# Revit family: QF_ELECTROLUXPROFESSIONAL_1LSN2C_WH6-6_E
name_source: partatom
category: Attrezzature speciali
units: mm (PartAtom-declared; Revit-internal decimal feet)

## family parameters
Basato su piano di lavoro = No
Condiviso = No
Punto di calcolo locali = No
Quota connettore circolare = Usa diametro
Sempre verticale = Sì
Taglio con vuoti quando caricato = No
Tipo di parte = Normale

## types (139) — shared parameters
Depth Actual = 595 mm  [stored 1.9521 ft]
Height Actual = 832 mm
Latent Heat Output = 0.0
Length Actual = 681 mm  [stored 2.23425 ft]
Modello = WH6-6
Produttore = Electrolux Professional
Sensible Heat Output = 0.0
URL = www.electroluxprofessional.com
Weight = 58
zero-valued in all types: Gas KW, Prospetto di default, Steam Pounds per Hour

## per-type parameters (varying)
| type | Cycle | Descrizione | Item Number | Phase | Volts | Watts |
| 9863430007 | 50 Hz | WASHER EXTRACTOR WH6-6 6KG/13LB EL 4,4KW 380-400/220-230/50/3N/1N COMPASS PRO 6H12 2.I/O 2xWATER POWDER+5xLIQ. QC VA... | 1L0ECD | 3 | 400 V | 2400 W |
| 9863430017 | 50 Hz | WASHER WH6-6 6KG EL 4,4KW 380-400/220-230/50/3N/1N COMPASS PRO 6L25 ML 2xWATER POWDER+5xLIQ. PUMP SILVER EXT.PM. 2.I/O | 1L0ECN | 3 | 400 V | 2400 W |
| 9863430207 | 60 Hz | WASHER EXTRACTOR WH6-6 MARINE 6KG/13LB EL 4,4KW 480/60/3 COMPASS PRO 6G07 2.I/O 2xWATER POWDER+5xLIQ. VALV.OPEN SLVR... | 1L0H5S | 3 | 480 V | 4600 W |
| 9863430217 | 60 Hz | Model: WH6-6 TYPE FAMILY W555H17 CH-EN MARINE 6KG EL 4KW 440/60/3 CPR 6G07 ML 2xWATER POWDER VALV.OPEN SILVER TRAFO | 1LT66F | 3 | 440 V | 4200 W |
| 9863430227 | 60 Hz | WASHER EXTRACTOR WH6-6 6KG/13LB EL 3,3KW 380-400/220-230/60/3N/1N COMPASS PRO 6G01 2.I/O 2xWATER POWDER+5xLIQ. VALV.... | 1LT6GB | 3 | 400 V | 3500 W |
| 9863430193 | 60 Hz | WASHER EXTRACTOR WH6-6 MARINE 6KG/13LB EL 4KW 440/60/3 COMPASS PRO 6G07 2xWATER POWDER VALV.OPEN SLVR/SLVR INS. TRAFO | 1L0GUG | 3 | 440 V | 4200 W |
| 9863430173 | 50 Hz | WASHER EXTRACTOR WH6-6 6KG/13LB NO HEAT 220-240/50/1N COMPASS PRO 6L25 2.I/O 2xWATER POWDER+5xLIQ. PUMP SST/SLVR | 1L999M | 1 | 240 V | 500 W |
| 9863430143 | 60 Hz | WASHER EXTRACTOR WH6-6 MARINE 6KG/13LB EL 4KW 440/60/3 COMPASS PRO 6G07 2xWATER POWDER VALV.OPEN SLVR/SLVR TRAFO | 1LA1AT | 3 | 440 V | 4200 W |
| 9863430153 | 50 Hz | WASHER EXTRACTOR WH6-6 6KG/13LB EL 2,8KW 220-240/50/1N COMPASS PRO 6G25 2.I/O 2xWATER POWDER+5xLIQ. PUMP SLVR/SLVR 1... | 1LA21G | 1 | 240 V | 3000 W |
| 9863430113 | 60 Hz | WASHER EXTRACTOR WH6-6 MARINE 6KG/13LB EL 4,4KW 380-400/220-230/60/3N/1N COMPASS PRO 6G27 2.I/O 2xWATER POWDER+5xLIQ... | 1LSNGY | 3 | 400 V | 2400 W |
| 9863430088 | 60 Hz | WASHER EXTRACTOR WH6-6 6KG/13LB EL 2,8KW 208-240/60/3 COMPASS PRO 6L01 2.I/O 2xWATER POWDER+5xLIQ. VALV.OPEN SLVR/SLVR | 1L0EL6 | 3 | 240 V | 3000 W |
| 9863430098 | 50 Hz | WASHER EXTRACTOR WH6-6 6KG/13LB EL 4,4KW 380-400/220-230/50/3N/1N COMPASS PRO 6H12 2.I/O 2xWATER POWDER+5xLIQ. QC PU... | 1LSNBM | 3 | 400 V | 2400 W |
| 9863430078 | 50 Hz | WASHER EXTRACTOR WH6-6 6KG/13LB EL 4,4KW 380-400/220-230/50/3N/1N COMPASS PRO 6A01 2xWATER POWDER VALV.OPEN SLVR/SLV... | 1LSN6B | 3 | 400 V | 2400 W |
| 9863430058 | 50 Hz | WASHER EXTRACTOR WH6-6 6KG/13LB EL 4,4KW 380-400/220-230/50/3N/1N COMPASS PRO 6A01 2xWATER POWDER EL.VALV.OPEN SLVR/... | 1L80G7 | 3 | 400 V | 2400 W |
| 9863430028 | 60 Hz | WASHER EXTRACTOR WH6-6 MARINE 6KG/13LB EL 4KW 440/60/3 COMPASS PRO 6G27 2xWATER POWDER PUMP SLVR/SLVR TRAFO | 1L0ED0 | 3 | 440 V | 4200 W |
| 9863430018 | 50 Hz | WASHER EXTRACTOR WH6-6 6KG/13LB EL 4,4KW 380-400/220-230/50/3N/1N COMPASS PRO 6M14 2.I/O 2xWATER POWDER+5xLIQ. QC EL... | 1L0ECP | 3 | 400 V | 2400 W |
| 9863430083 | 60 Hz | WASHER EXTRACTOR WH6-6 6KG/13LB EL 2,8KW 208-240/60/1 COMPASS PRO 6L01 2.I/O 2xWATER POWDER+5xLIQ. VALV.OPEN SLVR/SLVR | 1L0EK6 | 1 | 240 V | 3000 W |
| 9863430063 | 60 Hz | WASHER EXTRACTOR WH6-6 6KG/13LB NO HEAT 120/60/1N COMPASS PRO 6L33 2.I/O 2xWATER POWDER+5xLIQ. PUMP SLVR/SLVR TRAFO | 1L80GF | 1 | 120 V | 600 W |
| 9863430186 | 60 Hz | WASHER EXTRACTOR WH6-6 MARINE 6KG/13LB EL 4KW 440/60/3 COMPASS PRO 6G27 2xWATER POWDER PUMP SLVR/SLVR TRAFO | 1L0GTB | 3 | 440 V | 4200 W |
| 9863430023 | 50 Hz | WASHER EXTRACTOR WH6-6 6KG/13LB EL 4,4KW 380-400/220-230/50/3N/1N COMPASS PRO 6A01 2xWATER POWDER VALV.OPEN SLVR/SLV... | 1L0ECV | 3 | 400 V | 2400 W |
| 9863430166 | 60 Hz | WASHER EXTRACTOR WH6-6 MARINE 6KG/13LB EL 4,4KW 380-400/220-230/60/3N/1N COMPASS PRO 6G27 2xWATER POWDER PUMP SLVR/SLVR | 1L0GE6 | 3 | 400 V | 2400 W |
| 9863430176 | 50 Hz | WASHER EXTRACTOR WH6-6 6KG/13LB NO HEAT 220-240/50/1N COMPASS PRO 6G01 2xWATER POWDER VALV.OPEN SLVR/SLVR | 1L0GP0 | 1 | 240 V | 500 W |
| 9863430146 | 50 Hz | WASHER EXTRACTOR WH6-6 6KG/13LB EL 4,4KW 220-230/50/1N COMPASS PRO 6G01 2xWATER POWDER VALV.OPEN SLVR/SLVR | 1LA21A | 1 | 230 V | 4600 W |
| 9863430126 | 50 Hz | WASHER EXTRACTOR WH6-6 MARINE 6KG/13LB EL 3,3KW 380-400/50/3 COMPASS PRO 6G07 2.I/O 2xWATER POWDER+5xLIQ. EL.VALV.OP... | 1LSNRD | 3 | 400 V | 3500 W |
| 9863430196 | 50 Hz | WASHER EXTRACTOR WH6-6 6KG/13LB EL 3,3KW 380-400/220-230/50/3N/1N COMPASS PRO 6M17 2.I/O 2xWATER POWDER+5xLIQ. EL.VA... | 1LSPHT | 3 | 400 V | 3500 W |
| 9863430213 | 50 Hz | WASHER EXTRACTOR WH6-6 MARINE 6KG/13LB EL 3,6KW 380-415/50/3 COMPASS PRO 6G07 2.I/O 2xWATER POWDER+5xLIQ. QC VALV.OP... | 1LT65S | 3 | 415 V | 3800 W |
| 9863430064 | 60 Hz | WASHER EXTRACTOR WH6-6 6KG/13LB NO HEAT 120/60/1N COMPASS PRO 6L33 2xWATER POWDER VALV.OPEN SLVR/SLVR ELS-NETW. TRAFO | 1L80GG | 1 | 120 V | 600 W |
| 9863430044 | 50 Hz | WASHER EXTRACTOR WH6-6 6KG/13LB EL 3,3KW 200/50/60/3 COMPASS PRO 6H43 2.I/O 2xWATER POWDER+5xLIQ. VALV.OPEN SLVR/SLV... | 1L0EHE | 3 | 200 V | 3500 W |
| 9863430189 | 50 Hz | WASHER EXTRACTOR WH6-6 MARINE 6KG/13LB EL 3,3KW 380-400/50/3 COMPASS PRO 6G07 2.I/O 2xWATER POWDER+5xLIQ. EL.VALV.OP... | 1L0GTE | 3 | 400 V | 3500 W |
| 9863430024 | 60 Hz | WASHER EXTRACTOR WH6-6 MARINE 6KG/13LB EL 4KW 440/60/3 COMPASS PRO 6G07 2xWATER POWDER VALV.OPEN SLVR/SLVR INS. TRAFO | 1L0ECW | 3 | 440 V | 4200 W |
| 9863430034 | 60 Hz | WASHER WH6-6 MARINE 6KG EL 4KW 440/60/3 COMPASS PRO 6G07 ML 2xWATER POWDER+5xLIQ. VALV.OPEN SILVER QC 2.I/O TRAFO | 1L0ED5 | 3 | 440 V | 4200 W |
| 9863430169 | 60 Hz | WASHER EXTRACTOR WH6-6 MARINE 6KG/13LB EL 4,4KW 208-240/60/3 COMPASS PRO 6G27 2xWATER POWDER PUMP SLVR/SLVR | 1L0GHL | 3 | 240 V | 4600 W |
| 9863430014 | 50 Hz | WASHER EXTRACTOR WH6-6 6KG/13LB EL 4,4KW 380-400/220-230/50/3N/1N COMPASS PRO 6R01 2.I/O 2xWATER POWDER+5xLIQ. QC EL... | 1L0ECK | 3 | 400 V | 2400 W |
| 9863430199 | 50 Hz | WASHER EXTRACTOR WH6-6 6KG/13LB EL 3,3KW 200/50/60/3 COMPASS PRO 6H43 2xWATER POWDER VALV.OPEN SLVR/SLVR TRAFO | 1L0GY3 | 3 | 200 V | 3500 W |
| 9863430054 | 50 Hz | WASHER EXTRACTOR WH6-6 MARINE 6KG/13LB EL 3,3KW 380-400/50/3 COMPASS PRO 6G07 2.I/O 2xWATER POWDER+5xLIQ. VALV.OPEN ... | 1L80FY | 3 | 400 V | 3500 W |
| 9863430109 | 50 Hz | WASHER EXTRACTOR WH6-6 MARINE 6KG/13LB EL 4,4KW 220-230/50/3 COMPASS PRO 6G07 2xWATER POWDER VALV.OPEN SLVR/SLVR INS. | 1L0EPN | 3 | 230 V | 4600 W |
| 9863430119 | 50 Hz | WASHER EXTRACTOR WH6-6 6KG/13LB EL 4,4KW 220-230/50/3 COMPASS PRO 6A25 2.I/O 2xWATER POWDER+5xLIQ. PUMP SLVR/SLVR | 1L0FXT | 3 | 230 V | 4600 W |
| 9863430139 | 50 Hz | WASHER EXTRACTOR WH6-6 6KG/13LB EL 4,4KW 380-400/220-230/50/3N/1N COMPASS PRO 6G25 2.I/O 2xWATER POWDER+5xLIQ. QC PU... | 1LA215 | 3 | 400 V | 2400 W |
| 9863430149 | 50 Hz | WASHER EXTRACTOR WH6-6 MARINE 6KG/13LB EL 3,3KW 380-400/50/3 COMPASS PRO 6G07 2.I/O 2xWATER POWDER+5xLIQ. QC VALV.OP... | 1LA21C | 3 | 400 V | 3500 W |
| 9863430129 | 50 Hz | WASHER EXTRACTOR WH6-6 6KG/13LB EL 2,8KW 220-240/50/1N COMPASS PRO 6A25 2.I/O 2xWATER POWDER+5xLIQ. PUMP SLVR/SLVR | 1LSNXA | 1 | 240 V | 3000 W |
| 9863430182 | 50 Hz | WASHER EXTRACTOR WH6-6 6KG/13LB EL 4,4KW 380-400/220-230/50/3N/1N COMPASS PRO 6G01 2.I/O 2xWATER POWDER+5xLIQ. VALV.... | 1L0GT7 | 3 | 400 V | 2400 W |
| 9863430192 | 60 Hz | WASHER EXTRACTOR WH6-6 MARINE 6KG/13LB EL 4KW 440/60/3 COMPASS PRO 6G27 2.I/O 2xWATER POWDER+5xLIQ. PUMP SLVR/SLVR T... | 1L0GUF | 3 | 440 V | 4200 W |
| 9863430162 | 50 Hz | WASHER EXTRACTOR WH6-6 6KG/13LB NO HEAT 220-240/50/1N COMPASS PRO 6G01 2.I/O 2xWATER POWDER+5xLIQ. VALV.OPEN SLVR/SLVR | 1LSPAY | 1 | 240 V | 500 W |
| 9863430172 | 60 Hz | WASHER EXTRACTOR WH6-6 MARINE 6KG/13LB EL 4,4KW 220-230/60/3 COMPASS PRO 6G07 2.I/O 2xWATER POWDER+5xLIQ. VALV.OPEN ... | 1L0GL9 | 3 | 230 V | 4600 W |
| 9863430142 | 50 Hz | WASHER EXTRACTOR WH6-6 6KG/13LB EL 4,4KW 380-400/220-230/50/3N/1N COMPASS PRO 6L01 2.I/O 2xWATER POWDER+5xLIQ. VALV.... | 1LA217 | 3 | 400 V | 2400 W |
| 9863430218 | 50 Hz | Model: WH6-6 TYPE FAMILY W555H17 CH-EN 6 6KG EL 4,4KW 380-400/220-230/50/3N/1N COMPASS PRO 6G01 ML 2xWATER POWDER VALV.O | 1LT66K | 3 | 400 V | 2400 W |
| 9863430228 | 50 Hz | Model: WH6-6 TYPE FAMILY W555H17 CH-EN 6 6KG EL 4,4KW 380-400/220-230/50/3N/1N COMPASS PRO 6G01 ML 2xWATER POWDER VALV.O | 1LT6U8 | 3 | 230 V | 3500 W |
| 9863430080 | 50 Hz | WASHER EXTRACTOR WH6-6 6KG/13LB EL 4,4KW 380-400/220-230/50/3N/1N COMPASS PRO 6A01 2.I/O 2xWATER POWDER VALV.OPEN SL... | 1LSN6W | 3 | 400 V | 2400 W |
| 9863430070 | 60 Hz | WASHER EXTRACTOR WH6-6 MARINE 6KG/13LB EL 4KW 440/60/3 COMPASS PRO 6G07 2xWATER POWDER VALV.OPEN SST/SLVR INS. TRAFO | 1LSN53 | 3 | 440 V | 4200 W |
| 9863430185 | 50 Hz | WASHER EXTRACTOR WH6-6 6KG/13LB EL 4,4KW 240/50/1N COMPASS PRO 6H01 2.I/O 2xWATER POWDER+5xLIQ. EL.VALV.OPEN SLVR/SLVR | 1L0GTA | 1 | 240 V | 4600 W |
| 9863430195 | 50 Hz | WASHER EXTRACTOR WH6-6 6KG/13LB EL 4,4KW 380-400/220-230/50/3N/1N COMPASS PRO 6A01 2xWATER POWDER+ED QC VALV.OPEN SL... | 1L0GVZ | 3 | 400 V | 2400 W |
| 9863430165 | 60 Hz | WASHER EXTRACTOR WH6-6 6KG/13LB NO HEAT 120/60/1N COMPASS PRO 6S03 2xWATER POWDER PUMP SST/SLVR TRAFO | 1L0GDS | 1 | 120 V | 600 W |
| 9863430020 | 50 Hz | WASHER EXTRACTOR WH6-6 6KG/13LB EL 4,4KW 380-400/220-230/50/3N/1N COMPASS PRO 6H12 2.I/O 2xWATER POWDER+5xLIQ. VALV.... | 1L0ECS | 3 | 400 V | 2400 W |
| 9863430010 | 50 Hz | WASHER EXTRACTOR WH6-6 6KG/13LB EL 4,4KW 380-400/220-230/50/3N/1N COMPASS PRO 6M14 2.I/O 2xWATER POWDER+5xLIQ. EL.VA... | 1L0ECG | 3 | 400 V | 2400 W |
| 9863430050 | 60 Hz | WASHER EXTRACTOR WH6-6 MARINE 6KG/13LB EL 3,3KW 380-400/60/3 COMPASS PRO 6G27 2.I/O 2xWATER POWDER+5xLIQ. PUMP SLVR/... | 1L80EC | 3 | 400 V | 3500 W |
| 9863430135 | 60 Hz | WASHER EXTRACTOR WH6-6 MARINE 6KG/13LB EL 4KW 440/60/3 COMPASS PRO 6G27 2.I/O 2xWATER POWDER+5xLIQ. PUMP SST/SLVR TRAFO | 1L0G2H | 3 | 440 V | 4200 W |
| 9863430204 | 50 Hz | WASHER EXTRACTOR WH6-6 6KG/13LB NO HEAT 220-240/50/1N COMPASS PRO 6L01 2.I/O 2xWATER POWDER+5xLIQ. EL.VALV.OPEN SLVR... | 1L82AT | 1 | 240 V | 500 W |
| 9863430145 | 50 Hz | WASHER EXTRACTOR WH6-6 6KG/13LB EL 4,4KW 380-400/220-230/50/3N/1N COMPASS PRO 6G25 2.I/O 2xWATER POWDER+5xLIQ. PUMP ... | 1LA219 | 3 | 400 V | 2400 W |
| 9863430105 | 50 Hz | WASHER EXTRACTOR WH6-6 6KG/13LB EL 2,8KW 220-240/50/1N COMPASS PRO 6A25 2.I/O 2xWATER POWDER+5xLIQ. PUMP SLVR/SLVR E... | 1LSNFM | 1 | 240 V | 3000 W |
| 9863430125 | 60 Hz | WASHER EXTRACTOR WH6-6 MARINE 6KG/13LB EL 4KW 440/60/3 COMPASS PRO 6G07 2.I/O 2xWATER POWDER+5xLIQ. EL.VALV.OPEN SLV... | 1LSNRC | 3 | 440 V | 4200 W |
| 9863430175 | 60 Hz | WASHER EXTRACTOR WH6-6 MARINE 6KG/13LB EL 4,4KW 380-400/220-230/60/3N/1N COMPASS PRO 6G27 2.I/O 2xWATER POWDER+5xLIQ... | 1LSPE3 | 3 | 400 V | 2400 W |
| 9863430095 | 60 Hz | WASHER EXTRACTOR WH6-6 6KG/13LB NO HEAT 208-240/60/1 COMPASS PRO 6G01 2.I/O 2xWATER POWDER+5xLIQ. VALV.OPEN SLVR/SLVR | 1L0EN8 | 1 | 240 V | 500 W |
| 9863430075 | 50 Hz | WASHER WH6-6 6KG EL 4,4KW 380-400/220-230/50/3N/1N COMPASS PRO 6A01 ML 2xWATER POWDER+5xLIQ. VALV.OPEN SILVER ELS-NETW. | 1LSN5S | 3 | 400 V | 2400 W |
| 9863430055 | 60 Hz | WASHER EXTRACTOR WH6-6 6KG/13LB EL 2,2KW 208-240/60/1 COMPASS PRO 6G01 2.I/O 2xWATER POWDER+5xLIQ. VALV.OPEN SLVR/SLVR | 1LSN3W | 1 | 240 V | 2400 W |
| 9863430025 | 50 Hz | WASHER EXTRACTOR WH6-6 6KG/13LB EL 4,4KW 380-400/220-230/50/3N/1N COMPASS PRO 6A01 2xWATER POWDER VALV.OPEN SLVR/SLVR | 1L0ECX | 3 | 400 V | 2400 W |
| 9863430035 | 50 Hz | WASHER EXTRACTOR WH6-6 6KG/13LB EL 4,4KW 220-230/50/3 COMPASS PRO 6A01 2.I/O 2xWATER POWDER+5xLIQ. VALV.OPEN SLVR/SLVR | 1L0ED6 | 3 | 230 V | 4600 W |
| 9863430005 | 50 Hz | WASHER EXTRACTOR WH6-6 6KG/13LB EL 4,4KW 380-400/220-230/50/3N/1N COMPASS PRO 6M14 2.I/O 2xWATER POWDER+5xLIQ. QC EL... | 1L0ECB | 3 | 400 V | 2400 W |
| 9863430015 | 50 Hz | WASHER EXTRACTOR WH6-6 6KG/13LB EL 4,4KW 240/50/1N COMPASS PRO 6H01 2.I/O 2xWATER POWDER+5xLIQ. EL.VALV.OPEN SLVR/SLVR | 1L0ECL | 1 | 240 V | 4600 W |
| 9863430181 | 50 Hz | WASHER EXTRACTOR WH6-6 6KG/13LB EL 2,8KW 220-240/50/1N COMPASS PRO 6A25 2.I/O 2xWATER POWDER+5xLIQ. PUMP SLVR/SLVR E... | 1L0GT6 | 1 | 240 V | 3000 W |
| 9863430161 | 50 Hz | WASHER EXTRACTOR WH6-6 6KG/13LB EL 4,4KW 380-400/220-230/50/3N/1N COMPASS PRO 6M14 2xWATER POWDER+ED QC EL.VALV.OPEN... | 1LA1AA | 3 | 400 V | 2400 W |
| 9863430171 | 50 Hz | WASHER EXTRACTOR WH6-6 6KG/13LB EL 2,8KW 220-240/50/1N COMPASS PRO 6G01 2.I/O 2xWATER POWDER+5xLIQ. EL.VALV.OPEN SLV... | 1LA21H | 1 | 240 V | 3000 W |
| 9863430141 | 50 Hz | WASHER EXTRACTOR WH6-6 6KG/13LB EL 4,4KW 380-400/220-230/50/3N/1N COMPASS PRO 6G01 2xWATER POWDER VALV.OPEN SLVR/SLVR | 1L0GKG | 3 | 400 V | 2400 W |
| 9863430151 | 50 Hz | WASHER EXTRACTOR WH6-6 6KG/13LB EL 4,4KW 380-400/220-230/50/3N/1N COMPASS PRO 6L25 2.I/O 2xWATER POWDER+5xLIQ. PUMP ... | 1LA21E | 3 | 400 V | 2400 W |
| 9863430200 | 50 Hz | WASHER EXTRACTOR WH6-6 6KG/13LB NO HEAT 220-240/50/1N COMPASS PRO 6G05 2.I/O 2xWATER 5xLIQ. PUMP SLVR/SLVR | 1L8288 | 1 | 240 V | 500 W |
| 9863430210 | 60 Hz | WASHER EXTRACTOR WH6-6 6KG/13LB EL 4,4KW 380-400/220-230/60/3N/1N COMPASS PRO 6G01 2.I/O 2xWATER POWDER+5xLIQ. VALV.... | 1L0HDM | 3 | 400 V | 2400 W |
| 9863430091 | 60 Hz | WASHER EXTRACTOR WH6-6 MARINE 6KG/13LB EL 4KW 440/60/3 COMPASS PRO 6G27 2xWATER POWDER PUMP SST/SLVR TRAFO | 1L0ELK | 3 | 440 V | 4200 W |
| 9863430071 | 60 Hz | WASHER EXTRACTOR WH6-6 MARINE 6KG/13LB EL 4KW 440/60/3 COMPASS PRO 6G27 2.I/O 2xWATER POWDER+5xLIQ. PUMP SST/SLVR TRAFO | 1LSN54 | 3 | 440 V | 4200 W |
| 9863430184 | 50 Hz | WASHER EXTRACTOR WH6-6 6KG/13LB EL 4,4KW 380-400/220-230/50/3N/1N COMPASS PRO 6G25 2.I/O 2xWATER POWDER+5xLIQ. QC PU... | 1L0GT9 | 3 | 400 V | 2400 W |
| 9863430194 | 60 Hz | WASHER EXTRACTOR WH6-6 MARINE 6KG/13LB EL 4KW 440/60/3 COMPASS PRO 6G07 2xWATER POWDER VALV.OPEN SLVR/SLVR TRAFO | 1L0GUH | 3 | 440 V | 4200 W |
| 9863430021 | 60 Hz | WASHER EXTRACTOR WH6-6 MARINE 6KG/13LB EL 2,2KW 220-230/60/1N COMPASS PRO 6G07 2xWATER POWDER VALV.OPEN SLVR/SLVR | 1L0ECT | 1 | 230 V | 2400 W |
| 9863430031 | 50 Hz | WASHER EXTRACTOR WH6-6 6KG/13LB EL 4,4KW 220-230/50/3 COMPASS PRO 6M14 2.I/O 2xWATER POWDER+5xLIQ. QC EL.VALV.OPEN S... | 1L0ED2 | 3 | 230 V | 4600 W |
| 9863430011 | 50 Hz | WASHER EXTRACTOR WH6-6 6KG/13LB EL 4,4KW 380-400/220-230/50/3N/1N COMPASS PRO 6A01 2.I/O 2xWATER POWDER+5xLIQ. VALV.... | 1L0ECH | 3 | 400 V | 2400 W |
| 9863430164 | 50 Hz | WASHER EXTRACTOR WH6-6 6KG/13LB EL 4,4KW 380-400/220-230/50/3N/1N COMPASS PRO 6H01 2xWATER POWDER+ED VALV.OPEN SLVR/... | 1L0GDR | 3 | 400 V | 2400 W |
| 9863430051 | 60 Hz | WASHER EXTRACTOR WH6-6 6KG/13LB EL 4,4KW 415/60/3N COMPASS PRO 6G01 2.I/O 2xWATER POWDER+5xLIQ. VALV.OPEN SLVR/SLVR | 1L80FF | 3 | 415 V | 4600 W |
| 9863430134 | 50 Hz | WASHER EXTRACTOR WH6-6 6KG/13LB EL 4,4KW 380-400/220-230/50/3N/1N COMPASS PRO 6A01 2.I/O 2xWATER POWDER+5xLIQ. VALV.... | 1LA09G | 3 | 400 V | 2400 W |
| 9863430144 | 50 Hz | WASHER EXTRACTOR WH6-6 6KG/13LB NO HEAT 220-240/50/1N COMPASS PRO 6L01 2.I/O 2xWATER POWDER+5xLIQ. VALV.OPEN SLVR/SL... | 1LA218 | 1 | 240 V | 500 W |
| 9863430114 | 60 Hz | WASHER EXTRACTOR WH6-6 MARINE 6KG/13LB EL 4KW 440/60/3 COMPASS PRO 6G27 2.I/O 2xWATER POWDER+5xLIQ. PUMP SLVR/SLVR T... | 1LSNGZ | 3 | 440 V | 4200 W |
| 9863430124 | 60 Hz | WASHER EXTRACTOR WH6-6 MARINE 6KG/13LB EL 3,3KW 380-400/60/3 COMPASS PRO 6G07 2.I/O 2xWATER POWDER+5xLIQ. EL.VALV.OP... | 1LSNR7 | 3 | 400 V | 3500 W |
| 9863430174 | 50 Hz | WASHER EXTRACTOR WH6-6 6KG/13LB EL 4,4KW 380-400/220-230/50/3N/1N COMPASS PRO 6M26 2.I/O 2xWATER POWDER+5xLIQ. PUMP ... | 1LSPDZ | 3 | 400 V | 2400 W |
| 9863430160 | 60 Hz | WASHER EXTRACTOR WH6-6 6KG/13LB EL 3,3KW 380-400/60/3 COMPASS PRO 6G01 2xWATER POWDER VALV.OPEN SLVR/SLVR TRAFO | 1L0GD0 | 3 | 400 V | 3500 W |
| 9863430140 | 50 Hz | WASHER EXTRACTOR WH6-6 6KG/13LB EL 4,4KW 380-400/220-230/50/3N/1N COMPASS PRO 6G25 2xWATER POWDER PUMP SLVR/SLVR | 1LA216 | 3 | 400 V | 2400 W |
| 9863430221 | 50 Hz | Model: WH6-6 TYPE FAMILY W555H17 EL 4,4KW 380-400/220-230/50/3N/1N COMPASS PRO 6G25 CH-EN ML 2xWATER | 1LT6BB | 3 | 400 V | 2400 W |
| 9863430201 | 60 Hz | WASHER EXTRACTOR WH6-6 MARINE 6KG/13LB EL 4KW 440/60/3 COMPASS PRO 6G07 2.I/O 2xWATER POWDER+5xLIQ. VALV.OPEN SST/SL... | 1L0GZ0 | 3 | 440 V | 4200 W |
| 9863430110 | 50 Hz | WASHER EXTRACTOR WH6-6 6KG/13LB EL 4,4KW 380-400/220-230/50/3N/1N COMPASS PRO 6C01 2.I/O 2xWATER POWDER+5xLIQ. VALV.... | 1L0EPX | 3 | 400 V | 2400 W |
| 9863430089 | 60 Hz | WASHER EXTRACTOR WH6-6 MARINE 6KG/13LB EL 3,3KW 380-400/60/3 COMPASS PRO 6G27 2xWATER POWDER PUMP SLVR/SLVR TRAFO | 1LSN8K | 3 | 400 V | 3500 W |
| 9863430099 | 60 Hz | WASHER EXTRACTOR WH6-6 MARINE 6KG/13LB EL 2,2KW 220-230/60/1N COMPASS PRO 6G27 2xWATER POWDER PUMP SLVR/SLVR | 1LSNBV | 1 | 230 V | 2400 W |
| 9863430069 | 60 Hz | WASHER EXTRACTOR WH6-6 MARINE 6KG/13LB EL 2,2KW 220-230/60/1N COMPASS PRO 6G07 2.I/O 2xWATER POWDER+5xLIQ. VALV.OPEN... | 1LSN4H | 1 | 230 V | 2400 W |
| 9863430079 | 60 Hz | WASHER EXTRACTOR WH6-6 6KG/13LB EL 2,8KW 208-240/60/1 COMPASS PRO 6G25 2.I/O 2xWATER POWDER+5xLIQ. PUMP SLVR/SLVR | 1LSN6V | 1 | 240 V | 3000 W |
| 9863430059 | 50 Hz | WASHER EXTRACTOR WH6-6 6KG/13LB EL 4,4KW 380-400/220-230/50/3N/1N COMPASS PRO 6G25 2xWATER POWDER PUMP SLVR/SLVR INS. | 1L0EJ6 | 3 | 400 V | 2400 W |
| 9863430019 | 50 Hz | WASHER EXTRACTOR WH6-6 6KG/13LB EL 2,2KW 220-230/50/1N COMPASS PRO 6M14 2.I/O 2xWATER POWDER+5xLIQ. QC EL.VALV.OPEN ... | 1L0ECR | 1 | 230 V | 2400 W |
| 9863430188 | 60 Hz | WASHER EXTRACTOR WH6-6 MARINE 6KG/13LB EL 4KW 440/60/3 COMPASS PRO 6G07 2.I/O 2xWATER POWDER+5xLIQ. QC VALV.OPEN SLV... | 1L0GTD | 3 | 440 V | 4200 W |
| 9863430198 | 50 Hz | WASHER EXTRACTOR WH6-6 6KG/13LB NO HEAT 220-240/50/1N COMPASS PRO 6L25 2.I/O 2xWATER POWDER+5xLIQ. PUMP SLVR/SLVR EX... | 1LSPJL | 1 | 240 V | 500 W |
| 9863430168 | 60 Hz | WASHER EXTRACTOR WH6-6 6KG/13LB NO HEAT 220-240/60/1N COMPASS PRO 6G25 2.I/O 2xWATER POWDER+5xLIQ. QC PUMP SST/SLVR | 1L0GF3 | 1 | 240 V | 500 W |
| 9863430148 | 50 Hz | WASHER EXTRACTOR WH6-6 6KG/13LB EL 4,4KW 380-400/220-230/50/3N/1N COMPASS PRO 6R01 2.I/O 2xWATER POWDER+5xLIQ. EL.VA... | 1LA21B | 3 | 400 V | 2400 W |
| 9863430158 | 50 Hz | WASHER EXTRACTOR WH6-6 6KG/13LB EL 4,4KW 380-400/220-230/50/3N/1N COMPASS PRO 6M27 2.I/O 2xWATER POWDER+5xLIQ. PUMP ... | 1LSPG5 | 3 | 400 V | 2400 W |
| 9863430209 | 50 Hz | WASHER EXTRACTOR WH6-6 MARINE 6KG/13LB EL 3,3KW 380-400/50/3 COMPASS PRO 6G27 2.I/O 2xWATER POWDER+5xLIQ. PUMP SLVR/... | 1L0HBS | 3 | 400 V | 3500 W |
| 9863430128 | 50 Hz | WASHER EXTRACTOR WH6-6 MARINE 6KG/13LB EL 3,3KW 380-400/50/3 COMPASS PRO 6G27 2.I/O 2xWATER POWDER+5xLIQ. PUMP SLVR/... | 1LSNVW | 3 | 400 V | 3500 W |
| 9863430118 | 60 Hz | WASHER EXTRACTOR WH6-6 MARINE 6KG/13LB EL 4,4KW 380-400/220-230/60/3N/1N COMPASS PRO 6G27 2.I/O 2xWATER POWDER+5xLIQ... | 1L0FW7 | 3 | 400 V | 2400 W |
| 9863430219 | 50 Hz | WASHER EXTRACTOR WH6-6 6KG/13LB NO HEAT 220-240/50/1N COMPASS PRO 6L25 2.I/O 2xWATER POWDER PUMP SLVR/SLVR EXT.PM. | 1LT674 | 1 | 240 V | 500 W |
| 9863430205 | 50 Hz | WASHER EXTRACTOR WH6-6 6KG/13LB EL 2,2KW 220-230/50/1N COMPASS PRO 6G25 2.I/O 2xWATER POWDER+5xLIQ. PUMP SLVR/SLVR | 1LSPS2 | 1 | 230 V | 2400 W |
| 9863430086 | 60 Hz | WASHER EXTRACTOR WH6-6 6KG/13LB NO HEAT 208-240/60/1 COMPASS PRO 6L01 2.I/O 2xWATER POWDER+5xLIQ. VALV.OPEN SLVR/SLVR | 1L0EKA | 1 | 240 V | 500 W |
| 9863430076 | 50 Hz | WASHER EXTRACTOR WH6-6 6KG/13LB EL 4,4KW 380-400/220-230/50/3N/1N COMPASS PRO 6M14 2.I/O 2xWATER POWDER+5xLIQ. EL.VA... | 1LSN5T | 3 | 400 V | 2400 W |
| 9863430046 | 50 Hz | WASHER EXTRACTOR WH6-6 6KG/13LB EL 4,4KW 380-400/220-230/50/3N/1N COMPASS PRO 6A01 2.I/O 2xWATER POWDER+5xLIQ. VALV.... | 1L80DJ | 3 | 400 V | 2400 W |
| 9863430036 | 50 Hz | WASHER EXTRACTOR WH6-6 6KG/13LB EL 4,4KW 380-400/220-230/50/3N/1N COMPASS PRO 6M16 2.I/O 2xWATER POWDER+5xLIQ. EL.VA... | 1L0ED7 | 3 | 400 V | 2400 W |
| 9863430206 | 60 Hz | WASHER EXTRACTOR WH6-6 MARINE 6KG/13LB EL 4,4KW 220-230/60/3 COMPASS PRO 6G27 2.I/O 2xWATER POWDER+5xLIQ. PUMP SLVR/... | 1LSPS7 | 3 | 230 V | 4600 W |
| 9863430216 | 50 Hz | WASHER EXTRACTOR WH6-6 MARINE 6KG/13LB EL 3,3KW 380-400/50/3 COMPASS PRO 6G27 2.I/O 2xWATER POWDER+5xLIQ. PUMP SST/S... | 1LT664 | 3 | 400 V | 3500 W |
| 9863430082 | 50 Hz | WASHER EXTRACTOR WH6-6 MARINE 6KG/13LB EL 3,3KW 380-400/50/3 COMPASS PRO 6G27 2.I/O 2xWATER POWDER+5xLIQ. PUMP SLVR/... | 1L0EK2 | 3 | 400 V | 3500 W |
| 9863430092 | 60 Hz | WASHER EXTRACTOR WH6-6 MARINE 6KG/13LB EL 4,4KW 415/60/3N COMPASS PRO 6G27 2xWATER POWDER PUMP SLVR/SLVR | 1L0ELL | 3 | 415 V | 4600 W |
| 9863430062 | 60 Hz | WASHER EXTRACTOR WH6-6 MARINE 6KG/13LB EL 4,4KW 220-230/60/3 COMPASS PRO 6G27 2xWATER POWDER PUMP SLVR/SLVR | 1L80GC | 3 | 230 V | 4600 W |
| 9863430072 | 60 Hz | WASHER EXTRACTOR WH6-6 6KG/13LB EL 3,3KW 380-400/60/3 COMPASS PRO 6G25 2.I/O 2xWATER POWDER+5xLIQ. PUMP SLVR/SLVR TRAFO | 1L0EL4 | 3 | 400 V | 3500 W |
| 9863430187 | 50 Hz | WASHER EXTRACTOR WH6-6 6KG/13LB EL 4,4KW 380-400/220-230/50/3N/1N COMPASS PRO 6G25 2.I/O 2xWATER POWDER+5xLIQ. PUMP ... | 1L0GTC | 3 | 400 V | 2400 W |
| 9863430052 | 50 Hz | WASHER EXTRACTOR WH6-6 6KG/13LB EL 4,4KW 380-400/220-230/50/3N/1N COMPASS PRO 6C01 2.I/O 2xWATER POWDER+5xLIQ. VALV.... | 1L80FM | 3 | 400 V | 2400 W |
| 9863430167 | 60 Hz | WASHER EXTRACTOR WH6-6 MARINE 6KG/13LB EL 4,4KW 380-400/220-230/60/3N/1N COMPASS PRO 6L28 2.I/O 2xWATER POWDER+5xLIQ... | 1L0GE7 | 3 | 400 V | 2400 W |
| 9863430022 | 50 Hz | WASHER EXTRACTOR WH6-6 6KG/13LB EL 4,4KW 380-400/220-230/50/3N/1N COMPASS PRO 6H12 2xWATER POWDER+ED QC VALV.OPEN SL... | 1L0ECU | 3 | 400 V | 2400 W |
| 9863430147 | 50 Hz | WASHER EXTRACTOR WH6-6 6KG/13LB NO HEAT 220-240/50/1N COMPASS PRO 6L01 2.I/O 2xWATER POWDER VALV.OPEN SLVR/SLVR EXT.PM. | 1LA1D2 | 1 | 240 V | 500 W |
| 9863430157 | 50 Hz | WASHER EXTRACTOR WH6-6 6KG/13LB EL 4,4KW 380-400/220-230/50/3N/1N COMPASS PRO 6M17 2.I/O 2xWATER POWDER+5xLIQ. EL.VA... | 1L0GEZ | 3 | 400 V | 2400 W |
| 9863430202 | 50 Hz | WASHER EXTRACTOR WH6-6 6KG/13LB NO HEAT 220-240/50/1N COMPASS PRO 6G25 2xWATER POWDER PUMP SLVR/SLVR | 1L0GZF | 1 | 240 V | 500 W |
| 9863430127 | 50 Hz | WASHER EXTRACTOR WH6-6 6KG/13LB EL 3,3KW 380-400/50/3 COMPASS PRO 6M14 2.I/O 2xWATER POWDER+5xLIQ. EL.VALV.CLOSED SL... | 1L0FZ0 | 3 | 400 V | 3500 W |
| 9863430012 | 50 Hz | WASHER EXTRACTOR WH6-6 6KG/13LB EL 4,4KW 380-400/220-230/50/3N/1N COMPASS PRO 6G01 2.I/O 2xWATER POWDER+5xLIQ. VALV.... | 1L0ECJ | 3 | 400 V | 2400 W |
| 9863430117 | 50 Hz | WASHER EXTRACTOR WH6-6 6KG/13LB EL 4,4KW 380-400/220-230/50/3N/1N COMPASS PRO 6A01 2.I/O 2xWATER POWDER+5xLIQ. VALV.... | 1L0FW6 | 3 | 400 V | 2400 W |
| 9863430177 | 60 Hz | WASHER EXTRACTOR WH6-6 6KG/13LB NO HEAT 208-240/60/1 COMPASS PRO 6G25 2xWATER POWDER PUMP SLVR/SLVR | 1LD05J | 1 | 240 V | 500 W |
| 9863430197 | 50 Hz | WASHER EXTRACTOR WH6-6 6KG/13LB EL 3,3KW 380-400/220-230/50/3N/1N COMPASS PRO 6M27 2.I/O 2xWATER POWDER+5xLIQ. PUMP ... | 1LSPHU | 3 | 400 V | 3500 W |
| 9863430222 | 50 Hz | Model: WH6-6 TYPE FAMILY W555H17 EL 4,4KW 380-400/220-230/50/3N/1N COMPASS PRO 6G01 CH-EN ML 2xWATER | 1LT6BC | 3 | 400 V | 2400 W |
| 9863430087 | 60 Hz | WASHER EXTRACTOR WH6-6 MARINE 6KG/13LB EL 2,2KW 220-230/60/1N COMPASS PRO 6G27 2xWATER POWDER PUMP SLVR/SLVR | 1L0EL5 | 1 | 230 V | 2400 W |
| 9863430097 | 50 Hz | WASHER EXTRACTOR WH6-6 6KG/13LB EL 4,4KW 380-400/220-230/50/3N/1N COMPASS PRO 6H01 2xWATER POWDER+ED QC PUMP SLVR/SLVR | 1LSNAY | 3 | 400 V | 2400 W |
| 9863430077 | 50 Hz | WASHER EXTRACTOR WH6-6 6KG/13LB EL 4,4KW 380-400/220-230/50/3N/1N COMPASS PRO 6A25 2.I/O 2xWATER POWDER+5xLIQ. PUMP ... | 1LSN66 | 3 | 400 V | 2400 W |
| 9863430057 | 50 Hz | WASHER EXTRACTOR WH6-6 MARINE 6KG/13LB EL 2,2KW 220-230/50/1N COMPASS PRO 6G07 2xWATER POWDER VALV.OPEN SLVR/SLVR | 1L80G6 | 1 | 230 V | 2400 W |
| 9863430027 | 60 Hz | WASHER EXTRACTOR WH6-6 6KG/13LB EL 4,4KW 220-230/60/3 COMPASS PRO 6G01 2xWATER POWDER VALV.OPEN SLVR/SLVR | 1L0ECZ | 3 | 230 V | 4600 W |
| 9863430037 | 50 Hz | WASHER EXTRACTOR WH6-6 6KG/13LB EL 4,4KW 380-400/220-230/50/3N/1N COMPASS PRO 6M26 2.I/O 2xWATER POWDER+5xLIQ. PUMP ... | 1L0ED8 | 3 | 400 V | 2400 W |

note: [stored X ft] marks values corroborated as IEEE doubles in the binary element streams (Revit-internal decimal feet)

## geometry (parser evidence)
native form markers: Blend x2, Sweep x3
no freeform markers — native parametric forms only
